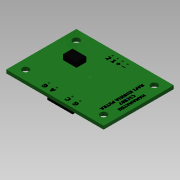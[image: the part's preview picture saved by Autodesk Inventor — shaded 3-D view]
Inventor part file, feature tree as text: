
AUTODESK INVENTOR PART (.ipt)
format: ipt  version: 2015 SP1 (Build 190203100, 203)  size: 166,912 bytes
history: native  units: mm
features: sketch x6, extrude x4
ambient origin geometry x8: Origin, YZ Plane, XZ Plane, XY Plane, X Axis, Y Axis, Z Axis, Center Point
bodies: Solid1 (feature_tree)
feature tree (10):
  extrude  "Extrusion1"  Depth=36.0mm
  extrude  "Extrusion2"  Depth=5.0mm
  extrude  "Extrusion3"  Depth=5.0mm
  sketch  "Sketch4"  dims[d17=1.27mm d18=2.5mm]
  extrude  "Extrusion4"  Depth=2.5mm
  sketch  "Sketch6"  dims[d20=2.54mm d21=1.0mm d22=4.0mm d23=1.0mm d24=4.0mm d25=1.7mm d26=0.0mm d27=13.0mm d28=13.0mm d29=12.0mm d30=0.0mm d31=7.0mm d32=5.0mm d33=2.5mm d34=0.0mm d35=5.0mm d36=5.0mm d37=5.0mm d38=5.0mm d39=0.1mm d40=0.0mm d41=12.0mm d43=40.0mm d44=26.0mm]
  sketch  "Sketch1"  dims[d0=50.0mm d1=36.0mm]
  sketch  "Sketch2"  dims[d10=3.5mm d12=5.0mm]
  sketch  "Sketch3"  dims[d13=5.0mm d16=1.0mm]
  sketch  "Sketch5"  dims[d19=1.0mm]
